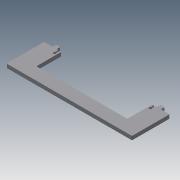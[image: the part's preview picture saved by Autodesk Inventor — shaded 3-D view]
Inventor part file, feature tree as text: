
AUTODESK INVENTOR PART (.ipt)
format: ipt  version: 2014 (Build 180170000, 170)  size: 157,184 bytes
history: native  units: mm
features: extrude x4, sketch x4, mirror x1, fillet x1
ambient origin geometry x8: Origin, YZ Plane, XZ Plane, XY Plane, X Axis, Y Axis, Z Axis, Center Point
bodies: Solid1 (feature_tree)
feature tree (10):
  extrude  "Extrusion1"  Depth=60.0mm
  extrude  "Extrusion2"  Depth=145.0mm
  extrude  "Extrusion3"  Depth=3.0mm TaperAngle=0.0deg
  extrude  "Extrusion4"  Depth=6.0mm
  mirror  "Mirror1"
  fillet  "Fillet1"  Radius=10.0mm
  sketch  "Sketch1"  dims[d0=200.0mm d1=60.0mm]
  sketch  "Sketch2"  dims[d2=6.0mm d3=0.0mm d4=145.0mm]
  sketch  "Sketch3"  dims[d5=20.0mm d6=3.0mm d7=0.0mm]
  sketch  "Sketch4"  dims[d8=6.25mm d9=6.0mm d10=10.0mm d11=0.0mm d12=2.1mm d13=4.1mm d14=9.0mm d15=6.0mm d16=1.8mm d17=10.0mm d18=0.0mm d19=1.0mm]
